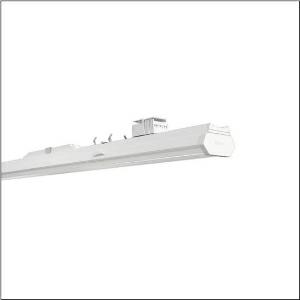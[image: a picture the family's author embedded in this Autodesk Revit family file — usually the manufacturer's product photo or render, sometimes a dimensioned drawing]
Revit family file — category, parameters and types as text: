
# Revit family: licross_r__21_protected_mo_52ts12dnd7xf_9118
name_source: partatom
category: Lighting Fixtures
units: mm (PartAtom-declared; Revit-internal decimal feet)

## family parameters
Cut with Voids When Loaded = No
Host = Face
Light Source = No
Part Type = Normal
Room Calculation Point = No
Round Connector Dimension = Use Diameter
Shared = No

## types (1)
- --- (1 x LED, 7240 lm, 60.9 W, 4000K)
    Apparent Load = 61 VA
    CIE Flux Codes = 54 82 95 97 100
    Color Rendering = 90
    Color Temperature = 4000K
    Default Elevation = 1800 mm
    Description = Licross® 21 Protected MO, luminaire insert, of sheet steel, galvanised, coil coated, white, length: 1.500mm, width: 90mm, height: 101mm, LED rated luminous flux: 7.240lm, light colour: 940, control gear: DALI 2, control gear: ECG DALI, with plug, 5-pole, with phase selection, mains connection: 220..240V, AC, 50/60Hz, halogen-free wiring, primary optical cover: cover, of PMMA, light emission: direct with ceiling illumination distribution, protection rating (complete): IP50, insulation class (complete): insulation class I (protective earthing), certification: CE, ENEC, VDE, UKCA, protection symbol: D if used in an environment with non-conductive dust loads with corresponding accessories, permissible ambient temperature for indoor applications: -25..+40°C, corresponds to IFS (International Featured Standards) requirements for safety and quality in the food industry, reducing of maximum allowable ambient temperature of 5°C with ceiling mounting, packaging unit: 1 piece
    Height = 92 mm
    Lamp = 1 x LED
    Lamp Light Flux = 7240 lm
    Lamp Power = 60.9 W
    Lamp count = 1
    Length = 1500 mm
    Luminous efficacy = 119 lm/W
    Manufacturer = Siteco
    ModVariant = No
    Model = 52TS12DND7XF
    Mounting Place = Ceiling
    Mounting Type = Pendant
    Number of Poles = 1
    OnlyDefault = Yes
    Power Factor = 1
    Product Name = Licross® 21 Protected MO
    Product group = luminaire insert
    ProductGroupID = 902
    Protection Class = Protection class I
    Protection Degree = IP 50
    RLX_Detail_Level = 1
    RlxData = <blob elided: 24065 chars, md5=8488ff19>
    Socket = socket
    Standby Power = 0 W
    System Light Flux = 7240 lm
    System Power = 61 W
    Type Comments = factory setting: luminous flux: 100 % | dim-lin: 254 | 405 mA
    Type Image = l_1256145.jpg
    URL = http://relux.com
    VarID = @adj_129575
    Voltage = 0 V
    Weight = 0.00 kg
    Width = 88 mm

## geometry (parser evidence)
native form markers: Blend x4, Sweep x10
no freeform markers — native parametric forms only
